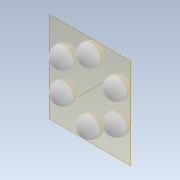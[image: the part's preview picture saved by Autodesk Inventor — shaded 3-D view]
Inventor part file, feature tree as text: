
AUTODESK INVENTOR PART (.ipt)
format: ipt  version: 2021 (Build 250183000, 183)  size: 124,928 bytes
history: native  units: mm
features: other x1, revolve x1, pattern_circular x1, sketch x1
ambient origin geometry x8: Origin, YZ Plane, XZ Plane, XY Plane, X Axis, Y Axis, Z Axis, Center Point
bodies: Body1 (feature_tree)
feature tree (4):
  other  "Sólido1"
  revolve  "Revolución1"  Angle=360.0deg
  pattern_circular  "Patrón circular1"  [2 undecoded]
  sketch  "Boceto2"  dims[d2=90.0deg d3=60.0mm d4=360.0deg]
note: 2 required parameter values undecoded (feature->parameter linkage not recoverable at this tier; creation-order binding heuristic only, values carry confidence <= 0.55)
